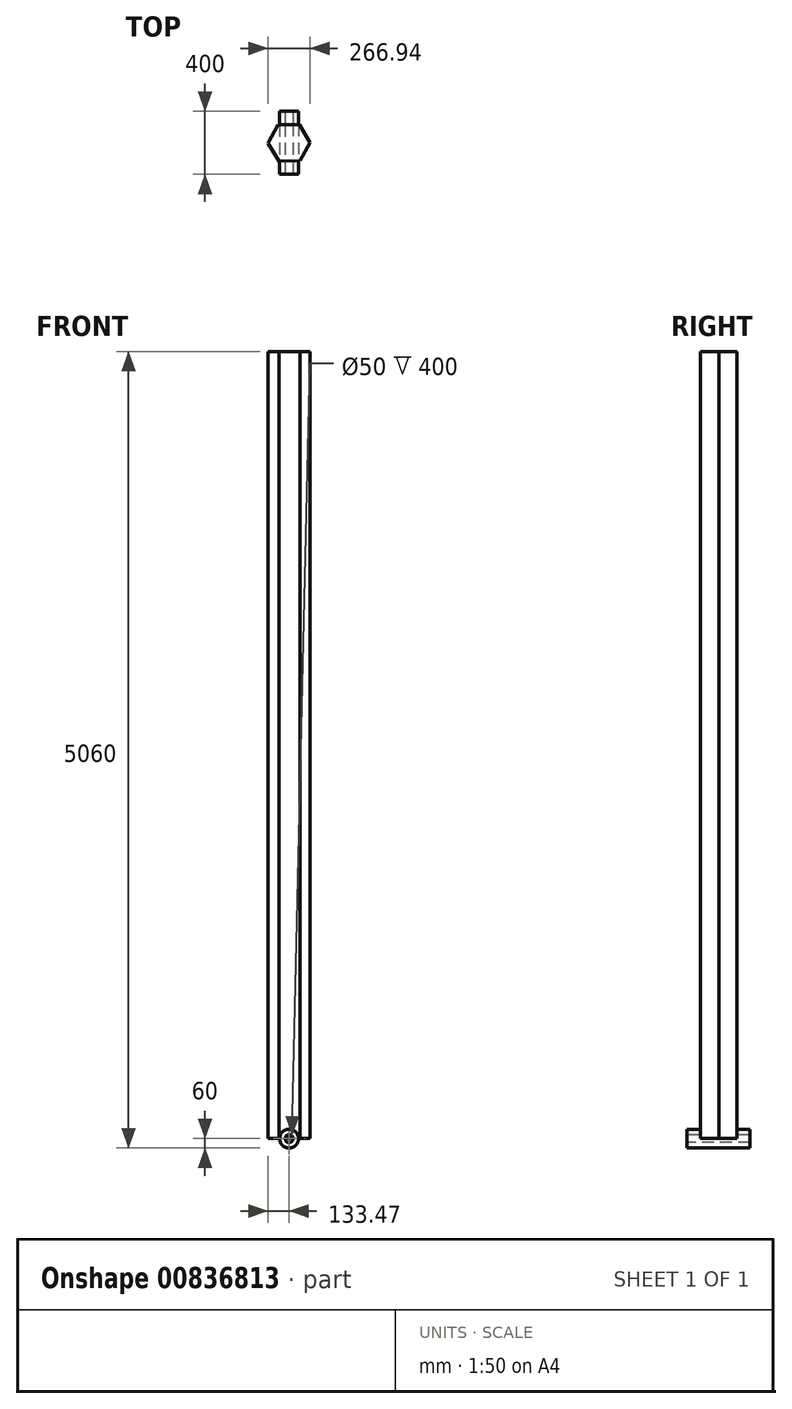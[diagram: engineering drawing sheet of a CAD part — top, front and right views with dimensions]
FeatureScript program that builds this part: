
annotation { "Feature Type Name" : "Feature", "Feature Type Description" : "" }
export const myFeature = defineFeature(function(context is Context, id is Id, definition is map)
    precondition{}
    {
        {
            var Q0;
            Q0=qCreatedBy(makeId("Front.planeOp"),FACE);
            var sketch = newSketch(context, id + "F0", { "sketchPlane" : qUnion([Q0])});
            skCircle(sketch, "E0", {"center": v(0, 0) * mm, "radius": 60 * mm});
            skCircle(sketch, "E1", {"center": v(0, 0) * mm, "radius": 25 * mm});
            skSolve(sketch);
        }
        {
            var Q0;
            Q0=makeQuery(id+"F0.imprint","IMPRINT",FACE,{"disambiguationData":[TD([[makeQuery(id+"F0.imprint","IMPRINT",EDGE,{"derivedFrom":sQuery(id+"F0.wireOp",EDGE,"E0")}),1.0]])]});
            extrude(context, id + "F1", {"entities" : qUnion([Q0]), "endBound" : BoundingType.SYMMETRIC, "oppositeDirection" : true, "depth" : 400 * mm, "offsetDistance" : 25 * mm});
        }
        {
            var Q0;
            Q0=qCreatedBy(makeId("Top.planeOp"),FACE);
            var sketch = newSketch(context, id + "F2", { "sketchPlane" : qUnion([Q0])});
            skCircle(sketch, "E2.cCircle", {"center": v(0, 0) * mm, "radius": 115.6 * mm, "construction": true});
            skLineSegment(sketch, "E2.0", {"start": v(64.85, 116.68) * mm, "end": v(133.47, 2.18) * mm});
            skLineSegment(sketch, "E2.1", {"start": v(133.47, 2.18) * mm, "end": v(68.62, -114.5) * mm});
            skLineSegment(sketch, "E2.2", {"start": v(68.62, -114.5) * mm, "end": v(-64.85, -116.68) * mm});
            skLineSegment(sketch, "E2.3", {"start": v(-64.85, -116.68) * mm, "end": v(-133.47, -2.18) * mm});
            skLineSegment(sketch, "E2.4", {"start": v(-133.47, -2.18) * mm, "end": v(-68.62, 114.5) * mm});
            skLineSegment(sketch, "E2.5", {"start": v(-68.62, 114.5) * mm, "end": v(64.85, 116.68) * mm});
            skPoint(sketch, "E2.0.midPoint", {"position": v(99.16, 59.43) * mm});
            skSolve(sketch);
        }
        {
            var Q0;
            Q0=makeQuery(id+"F2.imprint","IMPRINT",FACE,{"disambiguationData":[TD([[makeQuery(id+"F2.imprint","IMPRINT",EDGE,{"derivedFrom":sQuery(id+"F2.wireOp",EDGE,"E2.0")}),-1.0]])]});
            extrude(context, id + "F3", {"entities" : qUnion([Q0]), "operationType" : NewBodyOperationType.ADD, "depth" : 5000 * mm, "offsetDistance" : 25 * mm});
        }
    });
